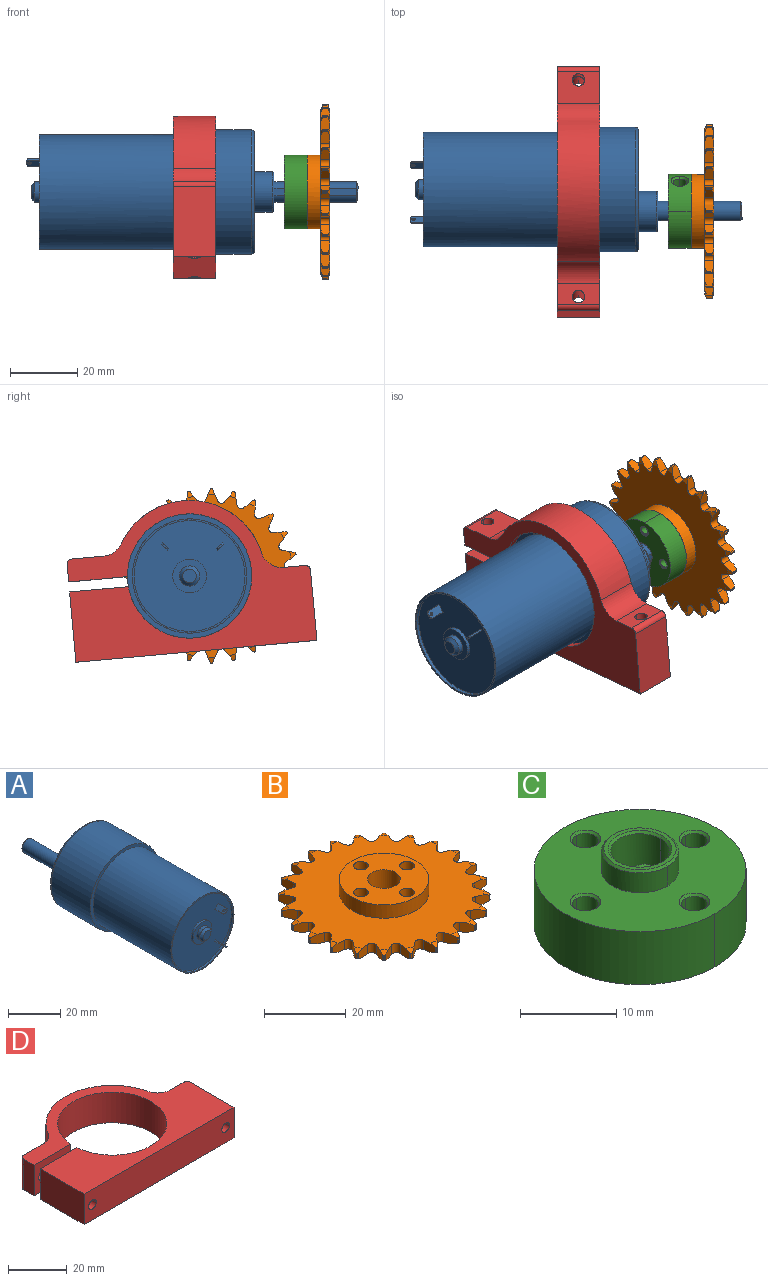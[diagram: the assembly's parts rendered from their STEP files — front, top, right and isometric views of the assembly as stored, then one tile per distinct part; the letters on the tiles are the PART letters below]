
ASSEMBLY  parts=4 mates=3
PART A: 37 faces, bbox 40.1x98.8x40.1 mm
  f0: cylinder r=3mm len=24.5mm, axis (0,-1,0), area 407.6mm2, adj f1,f3,f5
  f1: plane 24.5x2.16mm, normal (0,0,-1), area 53mm2, adj f0,f4,f5
  f2: plane 5x4.8mm, normal (0,1,0), area 19.4mm2, adj f3,f4
  f3: cone r=2.5mm half-angle=45deg, axis (0,-1,0), area 10.7mm2, adj f0,f2,f4
  f4: plane 2.17x0.51mm, normal (0,0.71,-0.71), area 1.5mm2, adj f1,f2,f3
  f5: plane 11x11mm, normal (0,1,0), area 67.1mm2, adj f0,f1,f36
  f6: plane 33x33mm, normal (0,-1,0), area 774.3mm2, adj f14,f15,f18,f19,f20,f21,f23,f24
  f7: plane 10x10mm, normal (0,-1,0), area 50.3mm2, adj f15,f16
  f8: plane 37x37mm, normal (0,-1,0), area 167.3mm2, adj f10,f12
  f9: plane 35x35mm, normal (0,1,0), area 849mm2, adj f11,f35
  f10: cylinder r=18.5mm len=37mm, axis (0,-1,0), area 2441mm2, adj f8,f35
  f11: cylinder r=6mm len=12mm, axis (0,-1,0), area 199.8mm2, adj f9,f36
  f12: cylinder r=17mm len=42mm, axis (0,1,0), area 4486.2mm2, adj f8,f13
  f13: plane 34x34mm, normal (0,-1,0), area 52.6mm2, adj f12,f14
  f14: cylinder r=16.5mm len=33mm, axis (0,-1,0), area 103.7mm2, adj f6,f13
  f15: cylinder r=5mm len=10mm, axis (0,1,0), area 31.4mm2, adj f6,f7
  f16: cylinder r=3mm len=6mm, axis (0,1,0), area 28.3mm2, adj f7,f30
  f17: plane 4x4mm, normal (0,-1,0), area 12.6mm2, adj f30
  f18: plane 4.5x0.35mm, normal (-0.71,0,-0.71), area 2.2mm2, adj f6,f19,f21,f33
  f19: plane 5x1.77mm, normal (0.71,0,-0.71), area 11.5mm2, adj f6,f18,f20,f22,f28,f33,f34
  f20: plane 4.5x0.35mm, normal (0.71,0,0.71), area 2.2mm2, adj f6,f19,f21,f34
  f21: plane 5x1.77mm, normal (-0.71,0,0.71), area 11.5mm2, adj f6,f18,f20,f22,f28,f33,f34
  f22: plane 1.41x1.41mm, normal (0,-1,0), area 0.8mm2, adj f19,f21,f33,f34
  f23: plane 4.5x0.35mm, normal (-0.71,0,0.71), area 2.3mm2, adj f6,f24,f26,f32
  f24: plane 5x1.77mm, normal (-0.71,0,-0.71), area 11.5mm2, adj f6,f23,f25,f27,f29,f31,f32
  f25: plane 4.5x0.35mm, normal (0.71,0,-0.71), area 2.2mm2, adj f6,f24,f26,f31
  f26: plane 5x1.77mm, normal (0.71,0,0.71), area 11.5mm2, adj f6,f23,f25,f27,f29,f31,f32
  f27: plane 1.41x1.41mm, normal (0,-1,0), area 0.7mm2, adj f24,f26,f31,f32
  f28: cylinder r=0.5mm len=1.06mm, axis (-0.71,0,0.71), area 1.6mm2, adj f19,f21
  f29: cylinder r=0.5mm len=1.06mm, axis (-0.71,0,-0.71), area 1.6mm2, adj f24,f26
  f30: cone r=2mm half-angle=45deg, axis (0,1,0), area 22.2mm2, adj f16,f17
  f31: plane 0.71x0.71mm, normal (0.5,-0.71,-0.5), area 0.4mm2, adj f24,f25,f26,f27
  f32: plane 0.71x0.71mm, normal (-0.5,-0.71,0.5), area 0.4mm2, adj f23,f24,f26,f27
  f33: plane 0.71x0.71mm, normal (-0.5,-0.71,-0.5), area 0.4mm2, adj f18,f19,f21,f22
  f34: plane 0.71x0.71mm, normal (0.5,-0.71,0.5), area 0.4mm2, adj f19,f20,f21,f22
  f35: torus R=17.5mm, axis (0,1,0), area 179mm2, adj f9,f10
  f36: torus R=5.5mm, axis (0,1,0), area 28.7mm2, adj f5,f11
PART B: 201 faces, bbox 52x52x6.8 mm
  f0: plane 48.65x48.65mm, normal (0,0,1), area 1311.2mm2, adj f1,f4,f7,f10,f13,f16,f19,f22
  f1: cone r=26mm half-angle=70deg, axis (0,0,-1), area 2.4mm2, adj f0,f2,f144,f146,f190,f193
  f2: cylinder r=26mm len=1.58mm, axis (0,0,1), area 0.5mm2, adj f1,f3,f190,f193
  f3: cone r=24.32mm half-angle=70deg, axis (0,0,1), area 2.4mm2, adj f2,f73,f144,f146,f190,f193
  f4: cone r=26mm half-angle=70deg, axis (0,0,-1), area 2.4mm2, adj f0,f5,f141,f143,f188,f191
  f5: cylinder r=26mm len=1.58mm, axis (0,0,1), area 0.5mm2, adj f4,f6,f188,f191
  f6: cone r=24.32mm half-angle=70deg, axis (0,0,1), area 2.4mm2, adj f5,f73,f141,f143,f188,f191
  f7: cone r=26mm half-angle=70deg, axis (0,0,-1), area 2.4mm2, adj f0,f8,f138,f140,f186,f189
  f8: cylinder r=26mm len=1.58mm, axis (0,0,1), area 0.5mm2, adj f7,f9,f186,f189
  f9: cone r=24.32mm half-angle=70deg, axis (0,0,1), area 2.4mm2, adj f8,f73,f138,f140,f186,f189
  f10: cone r=26mm half-angle=70deg, axis (0,0,-1), area 2.4mm2, adj f0,f11,f135,f137,f184,f187
  f11: cylinder r=26mm len=1.58mm, axis (0,0,1), area 0.5mm2, adj f10,f12,f184,f187
  f12: cone r=24.32mm half-angle=70deg, axis (0,0,1), area 2.4mm2, adj f11,f73,f135,f137,f184,f187
  f13: cone r=26mm half-angle=70deg, axis (0,0,-1), area 2.4mm2, adj f0,f14,f132,f134,f182,f185
  f14: cylinder r=26mm len=1.58mm, axis (0,0,1), area 0.5mm2, adj f13,f15,f182,f185
  f15: cone r=24.32mm half-angle=70deg, axis (0,0,1), area 2.4mm2, adj f14,f73,f132,f134,f182,f185
  f16: cone r=26mm half-angle=70deg, axis (0,0,-1), area 2.4mm2, adj f0,f17,f129,f131,f180,f183
  f17: cylinder r=26mm len=1.58mm, axis (0,0,1), area 0.5mm2, adj f16,f18,f180,f183
  f18: cone r=24.32mm half-angle=70deg, axis (0,0,1), area 2.4mm2, adj f17,f73,f129,f131,f180,f183
  f19: cone r=26mm half-angle=70deg, axis (0,0,-1), area 2.4mm2, adj f0,f20,f126,f128,f178,f181
  f20: cylinder r=26mm len=1.58mm, axis (0,0,1), area 0.5mm2, adj f19,f21,f178,f181
  f21: cone r=24.32mm half-angle=70deg, axis (0,0,1), area 2.4mm2, adj f20,f73,f126,f128,f178,f181
  f22: cone r=26mm half-angle=70deg, axis (0,0,-1), area 2.4mm2, adj f0,f23,f123,f125,f176,f179
  f23: cylinder r=26mm len=1.58mm, axis (0,0,1), area 0.5mm2, adj f22,f24,f176,f179
  f24: cone r=24.32mm half-angle=70deg, axis (0,0,1), area 2.4mm2, adj f23,f73,f123,f125,f176,f179
  f25: cone r=26mm half-angle=70deg, axis (0,0,-1), area 2.4mm2, adj f0,f26,f120,f122,f174,f177
  f26: cylinder r=26mm len=1.58mm, axis (0,0,1), area 0.5mm2, adj f25,f27,f174,f177
  f27: cone r=24.32mm half-angle=70deg, axis (0,0,1), area 2.4mm2, adj f26,f73,f120,f122,f174,f177
  f28: cone r=26mm half-angle=70deg, axis (0,0,-1), area 2.4mm2, adj f0,f29,f117,f119,f172,f175
  f29: cylinder r=26mm len=1.58mm, axis (0,0,1), area 0.5mm2, adj f28,f30,f172,f175
  f30: cone r=24.32mm half-angle=70deg, axis (0,0,1), area 2.4mm2, adj f29,f73,f117,f119,f172,f175
  f31: cone r=26mm half-angle=70deg, axis (0,0,-1), area 2.4mm2, adj f0,f32,f114,f116,f170,f173
  f32: cylinder r=26mm len=1.58mm, axis (0,0,1), area 0.5mm2, adj f31,f33,f170,f173
  f33: cone r=24.32mm half-angle=70deg, axis (0,0,1), area 2.4mm2, adj f32,f73,f114,f116,f170,f173
  f34: cone r=26mm half-angle=70deg, axis (0,0,-1), area 2.4mm2, adj f0,f35,f111,f113,f168,f171
  f35: cylinder r=26mm len=1.58mm, axis (0,0,1), area 0.5mm2, adj f34,f36,f168,f171
  f36: cone r=24.32mm half-angle=70deg, axis (0,0,1), area 2.4mm2, adj f35,f73,f111,f113,f168,f171
  f37: cone r=26mm half-angle=70deg, axis (0,0,-1), area 2.4mm2, adj f0,f38,f108,f110,f166,f169
  f38: cylinder r=26mm len=1.58mm, axis (0,0,1), area 0.5mm2, adj f37,f39,f166,f169
  f39: cone r=24.32mm half-angle=70deg, axis (0,0,1), area 2.4mm2, adj f38,f73,f108,f110,f166,f169
  f40: cone r=26mm half-angle=70deg, axis (0,0,-1), area 2.4mm2, adj f0,f41,f105,f107,f164,f167
  f41: cylinder r=26mm len=1.58mm, axis (0,0,1), area 0.5mm2, adj f40,f42,f164,f167
  f42: cone r=24.32mm half-angle=70deg, axis (0,0,1), area 2.4mm2, adj f41,f73,f105,f107,f164,f167
  f43: cone r=26mm half-angle=70deg, axis (0,0,-1), area 2.4mm2, adj f0,f44,f102,f104,f162,f165
  f44: cylinder r=26mm len=1.58mm, axis (0,0,1), area 0.5mm2, adj f43,f45,f162,f165
  f45: cone r=24.32mm half-angle=70deg, axis (0,0,1), area 2.4mm2, adj f44,f73,f102,f104,f162,f165
  f46: cone r=26mm half-angle=70deg, axis (0,0,-1), area 2.4mm2, adj f0,f47,f99,f101,f160,f163
  f47: cylinder r=26mm len=1.58mm, axis (0,0,1), area 0.5mm2, adj f46,f48,f160,f163
  f48: cone r=24.32mm half-angle=70deg, axis (0,0,1), area 2.4mm2, adj f47,f73,f99,f101,f160,f163
  f49: cone r=26mm half-angle=70deg, axis (0,0,-1), area 2.4mm2, adj f0,f50,f96,f98,f158,f161
  f50: cylinder r=26mm len=1.58mm, axis (0,0,1), area 0.5mm2, adj f49,f51,f158,f161
  f51: cone r=24.32mm half-angle=70deg, axis (0,0,1), area 2.4mm2, adj f50,f73,f96,f98,f158,f161
  f52: cone r=26mm half-angle=70deg, axis (0,0,-1), area 2.4mm2, adj f0,f53,f93,f95,f156,f159
  f53: cylinder r=26mm len=1.58mm, axis (0,0,1), area 0.5mm2, adj f52,f54,f156,f159
  f54: cone r=24.32mm half-angle=70deg, axis (0,0,1), area 2.4mm2, adj f53,f73,f93,f95,f156,f159
  f55: cone r=26mm half-angle=70deg, axis (0,0,-1), area 2.4mm2, adj f0,f56,f90,f92,f154,f157
  f56: cylinder r=26mm len=1.58mm, axis (0,0,1), area 0.5mm2, adj f55,f57,f154,f157
  f57: cone r=24.32mm half-angle=70deg, axis (0,0,1), area 2.4mm2, adj f56,f73,f90,f92,f154,f157
  f58: cone r=26mm half-angle=70deg, axis (0,0,-1), area 2.4mm2, adj f0,f59,f87,f89,f152,f155
  f59: cylinder r=26mm len=1.58mm, axis (0,0,1), area 0.5mm2, adj f58,f60,f152,f155
  f60: cone r=24.32mm half-angle=70deg, axis (0,0,1), area 2.4mm2, adj f59,f73,f87,f89,f152,f155
  f61: cone r=26mm half-angle=70deg, axis (0,0,-1), area 2.4mm2, adj f0,f62,f84,f86,f150,f153
  f62: cylinder r=26mm len=1.58mm, axis (0,0,1), area 0.5mm2, adj f61,f63,f150,f153
  f63: cone r=24.32mm half-angle=70deg, axis (0,0,1), area 2.4mm2, adj f62,f73,f84,f86,f150,f153
  f64: cone r=26mm half-angle=70deg, axis (0,0,-1), area 2.4mm2, adj f0,f65,f81,f83,f148,f151
  f65: cylinder r=26mm len=1.58mm, axis (0,0,1), area 0.5mm2, adj f64,f66,f148,f151
  f66: cone r=24.32mm half-angle=70deg, axis (0,0,1), area 2.4mm2, adj f65,f73,f81,f83,f148,f151
  f67: cone r=26mm half-angle=70deg, axis (0,0,-1), area 2.4mm2, adj f0,f68,f76,f77,f80,f149
  f68: cylinder r=26mm len=1.58mm, axis (0,0,1), area 0.5mm2, adj f67,f69,f77,f149
  f69: cone r=24.32mm half-angle=70deg, axis (0,0,1), area 2.4mm2, adj f68,f73,f76,f77,f80,f149
  f70: cone r=26mm half-angle=70deg, axis (0,0,-1), area 2.4mm2, adj f0,f71,f75,f78,f147,f192
  f71: cylinder r=26mm len=1.58mm, axis (0,0,1), area 0.5mm2, adj f70,f72,f78,f192
  f72: cone r=24.32mm half-angle=70deg, axis (0,0,1), area 2.4mm2, adj f71,f73,f75,f78,f147,f192
  f73: plane 48.65x48.65mm, normal (0,0,-1), area 1600.4mm2, adj f3,f6,f9,f12,f15,f18,f21,f24
  f74: cylinder r=1.25mm len=2.8mm, axis (0,0,1), area 7.2mm2, adj f0,f73,f75,f76
  f75: plane 2.99x2.8mm, normal (0.78,0.62,0), area 9.7mm2, adj f0,f70,f72,f73,f74,f78
  f76: plane 3.5x2.8mm, normal (-0.92,0.4,0), area 9.7mm2, adj f0,f67,f69,f73,f74,f77
  f77: cylinder r=0.2mm len=1.67mm, axis (0,0,1), area 0.4mm2, adj f67,f68,f69,f76
  f78: cylinder r=0.2mm len=1.67mm, axis (0,0,1), area 0.4mm2, adj f70,f71,f72,f75
  f79: cylinder r=1.25mm len=2.8mm, axis (0,0,1), area 7.2mm2, adj f0,f73,f80,f81
  f80: plane 3.5x2.8mm, normal (0.92,0.4,0), area 9.7mm2, adj f0,f67,f69,f73,f79,f149
  f81: plane 2.99x2.8mm, normal (-0.78,0.62,0), area 9.7mm2, adj f0,f64,f66,f73,f79,f148
  f82: cylinder r=1.25mm len=2.8mm, axis (0,0,1), area 7.2mm2, adj f0,f73,f83,f84
  f83: plane 3.77x2.8mm, normal (0.99,0.15,0), area 9.7mm2, adj f0,f64,f66,f73,f82,f151
  f84: plane 3.06x2.8mm, normal (-0.6,0.8,0), area 9.7mm2, adj f0,f61,f63,f73,f82,f150
  f85: cylinder r=1.25mm len=2.8mm, axis (0,0,1), area 7.2mm2, adj f0,f73,f86,f87
  f86: plane 3.79x2.8mm, normal (0.99,-0.12,0), area 9.7mm2, adj f0,f61,f63,f73,f85,f153
  f87: plane 3.54x2.8mm, normal (-0.37,0.93,0), area 9.7mm2, adj f0,f58,f60,f73,f85,f152
  f88: cylinder r=1.25mm len=2.8mm, axis (0,0,1), area 7.2mm2, adj f0,f73,f89,f90
  f89: plane 3.54x2.8mm, normal (0.93,-0.37,0), area 9.7mm2, adj f0,f58,f60,f73,f88,f155
  f90: plane 3.79x2.8mm, normal (-0.12,0.99,0), area 9.7mm2, adj f0,f55,f57,f73,f88,f154
  f91: cylinder r=1.25mm len=2.8mm, axis (0,0,1), area 7.2mm2, adj f0,f73,f92,f93
  f92: plane 3.06x2.8mm, normal (0.8,-0.6,0), area 9.7mm2, adj f0,f55,f57,f73,f91,f157
  f93: plane 3.77x2.8mm, normal (0.15,0.99,0), area 9.7mm2, adj f0,f52,f54,f73,f91,f156
  f94: cylinder r=1.25mm len=2.8mm, axis (0,0,1), area 7.2mm2, adj f0,f73,f95,f96
  f95: plane 2.99x2.8mm, normal (0.62,-0.78,0), area 9.7mm2, adj f0,f52,f54,f73,f94,f159
  f96: plane 3.5x2.8mm, normal (0.4,0.92,0), area 9.7mm2, adj f0,f49,f51,f73,f94,f158
  f97: cylinder r=1.25mm len=2.8mm, axis (0,0,1), area 7.2mm2, adj f0,f73,f98,f99
  f98: plane 3.5x2.8mm, normal (0.4,-0.92,0), area 9.7mm2, adj f0,f49,f51,f73,f97,f161
  f99: plane 2.99x2.8mm, normal (0.62,0.78,0), area 9.7mm2, adj f0,f46,f48,f73,f97,f160
  f100: cylinder r=1.25mm len=2.8mm, axis (0,0,1), area 7.2mm2, adj f0,f73,f101,f102
  f101: plane 3.77x2.8mm, normal (0.15,-0.99,0), area 9.7mm2, adj f0,f46,f48,f73,f100,f163
  f102: plane 3.06x2.8mm, normal (0.8,0.6,0), area 9.7mm2, adj f0,f43,f45,f73,f100,f162
  f103: cylinder r=1.25mm len=2.8mm, axis (0,0,1), area 7.2mm2, adj f0,f73,f104,f105
  f104: plane 3.79x2.8mm, normal (-0.12,-0.99,0), area 9.7mm2, adj f0,f43,f45,f73,f103,f165
  f105: plane 3.54x2.8mm, normal (0.93,0.37,0), area 9.7mm2, adj f0,f40,f42,f73,f103,f164
  f106: cylinder r=1.25mm len=2.8mm, axis (0,0,1), area 7.2mm2, adj f0,f73,f107,f108
  f107: plane 3.54x2.8mm, normal (-0.37,-0.93,0), area 9.7mm2, adj f0,f40,f42,f73,f106,f167
  f108: plane 3.79x2.8mm, normal (0.99,0.12,0), area 9.7mm2, adj f0,f37,f39,f73,f106,f166
  f109: cylinder r=1.25mm len=2.8mm, axis (0,0,1), area 7.2mm2, adj f0,f73,f110,f111
  f110: plane 3.06x2.8mm, normal (-0.6,-0.8,0), area 9.7mm2, adj f0,f37,f39,f73,f109,f169
  f111: plane 3.77x2.8mm, normal (0.99,-0.15,0), area 9.7mm2, adj f0,f34,f36,f73,f109,f168
  f112: cylinder r=1.25mm len=2.8mm, axis (0,0,1), area 7.2mm2, adj f0,f73,f113,f114
  f113: plane 2.99x2.8mm, normal (-0.78,-0.62,0), area 9.7mm2, adj f0,f34,f36,f73,f112,f171
  f114: plane 3.5x2.8mm, normal (0.92,-0.4,0), area 9.7mm2, adj f0,f31,f33,f73,f112,f170
  f115: cylinder r=1.25mm len=2.8mm, axis (0,0,1), area 7.2mm2, adj f0,f73,f116,f117
  f116: plane 3.5x2.8mm, normal (-0.92,-0.4,0), area 9.7mm2, adj f0,f31,f33,f73,f115,f173
  f117: plane 2.99x2.8mm, normal (0.78,-0.62,0), area 9.7mm2, adj f0,f28,f30,f73,f115,f172
  f118: cylinder r=1.25mm len=2.8mm, axis (0,0,1), area 7.2mm2, adj f0,f73,f119,f120
  f119: plane 3.77x2.8mm, normal (-0.99,-0.15,0), area 9.7mm2, adj f0,f28,f30,f73,f118,f175
  f120: plane 3.06x2.8mm, normal (0.6,-0.8,0), area 9.7mm2, adj f0,f25,f27,f73,f118,f174
  f121: cylinder r=1.25mm len=2.8mm, axis (0,0,1), area 7.2mm2, adj f0,f73,f122,f123
  f122: plane 3.79x2.8mm, normal (-0.99,0.12,0), area 9.7mm2, adj f0,f25,f27,f73,f121,f177
  f123: plane 3.54x2.8mm, normal (0.37,-0.93,0), area 9.7mm2, adj f0,f22,f24,f73,f121,f176
  f124: cylinder r=1.25mm len=2.8mm, axis (0,0,1), area 7.2mm2, adj f0,f73,f125,f126
  f125: plane 3.54x2.8mm, normal (-0.93,0.37,0), area 9.7mm2, adj f0,f22,f24,f73,f124,f179
  f126: plane 3.79x2.8mm, normal (0.12,-0.99,0), area 9.7mm2, adj f0,f19,f21,f73,f124,f178
  f127: cylinder r=1.25mm len=2.8mm, axis (0,0,1), area 7.2mm2, adj f0,f73,f128,f129
  f128: plane 3.06x2.8mm, normal (-0.8,0.6,0), area 9.7mm2, adj f0,f19,f21,f73,f127,f181
  f129: plane 3.77x2.8mm, normal (-0.15,-0.99,0), area 9.7mm2, adj f0,f16,f18,f73,f127,f180
  f130: cylinder r=1.25mm len=2.8mm, axis (0,0,1), area 7.2mm2, adj f0,f73,f131,f132
  f131: plane 2.99x2.8mm, normal (-0.62,0.78,0), area 9.7mm2, adj f0,f16,f18,f73,f130,f183
  f132: plane 3.5x2.8mm, normal (-0.4,-0.92,0), area 9.7mm2, adj f0,f13,f15,f73,f130,f182
  f133: cylinder r=1.25mm len=2.8mm, axis (0,0,1), area 7.2mm2, adj f0,f73,f134,f135
  f134: plane 3.5x2.8mm, normal (-0.4,0.92,0), area 9.7mm2, adj f0,f13,f15,f73,f133,f185
  f135: plane 2.99x2.8mm, normal (-0.62,-0.78,0), area 9.7mm2, adj f0,f10,f12,f73,f133,f184
  f136: cylinder r=1.25mm len=2.8mm, axis (0,0,1), area 7.2mm2, adj f0,f73,f137,f138
  f137: plane 3.77x2.8mm, normal (-0.15,0.99,0), area 9.7mm2, adj f0,f10,f12,f73,f136,f187
  f138: plane 3.06x2.8mm, normal (-0.8,-0.6,0), area 9.7mm2, adj f0,f7,f9,f73,f136,f186
  f139: cylinder r=1.25mm len=2.8mm, axis (0,0,1), area 7.2mm2, adj f0,f73,f140,f141
  f140: plane 3.79x2.8mm, normal (0.12,0.99,0), area 9.7mm2, adj f0,f7,f9,f73,f139,f189
  f141: plane 3.54x2.8mm, normal (-0.93,-0.37,0), area 9.7mm2, adj f0,f4,f6,f73,f139,f188
  f142: cylinder r=1.25mm len=2.8mm, axis (0,0,1), area 7.2mm2, adj f0,f73,f143,f144
  f143: plane 3.54x2.8mm, normal (0.37,0.93,0), area 9.7mm2, adj f0,f4,f6,f73,f142,f191
  f144: plane 3.79x2.8mm, normal (-0.99,-0.12,0), area 9.7mm2, adj f0,f1,f3,f73,f142,f190
  f145: cylinder r=1.25mm len=2.8mm, axis (0,0,1), area 7.2mm2, adj f0,f73,f146,f147
  f146: plane 3.06x2.8mm, normal (0.6,0.8,0), area 9.7mm2, adj f0,f1,f3,f73,f145,f193
  f147: plane 3.77x2.8mm, normal (-0.99,0.15,0), area 9.7mm2, adj f0,f70,f72,f73,f145,f192
  f148: cylinder r=0.2mm len=1.67mm, axis (0,0,1), area 0.4mm2, adj f64,f65,f66,f81
  f149: cylinder r=0.2mm len=1.67mm, axis (0,0,1), area 0.4mm2, adj f67,f68,f69,f80
  f150: cylinder r=0.2mm len=1.67mm, axis (0,0,1), area 0.4mm2, adj f61,f62,f63,f84
  f151: cylinder r=0.2mm len=1.67mm, axis (0,0,1), area 0.4mm2, adj f64,f65,f66,f83
  f152: cylinder r=0.2mm len=1.67mm, axis (0,0,1), area 0.4mm2, adj f58,f59,f60,f87
  f153: cylinder r=0.2mm len=1.67mm, axis (0,0,1), area 0.4mm2, adj f61,f62,f63,f86
  f154: cylinder r=0.2mm len=1.67mm, axis (0,0,1), area 0.4mm2, adj f55,f56,f57,f90
  f155: cylinder r=0.2mm len=1.67mm, axis (0,0,1), area 0.4mm2, adj f58,f59,f60,f89
  f156: cylinder r=0.2mm len=1.67mm, axis (0,0,1), area 0.4mm2, adj f52,f53,f54,f93
  f157: cylinder r=0.2mm len=1.67mm, axis (0,0,1), area 0.4mm2, adj f55,f56,f57,f92
  f158: cylinder r=0.2mm len=1.67mm, axis (0,0,1), area 0.4mm2, adj f49,f50,f51,f96
  f159: cylinder r=0.2mm len=1.67mm, axis (0,0,1), area 0.4mm2, adj f52,f53,f54,f95
  f160: cylinder r=0.2mm len=1.67mm, axis (0,0,1), area 0.4mm2, adj f46,f47,f48,f99
  f161: cylinder r=0.2mm len=1.67mm, axis (0,0,1), area 0.4mm2, adj f49,f50,f51,f98
  f162: cylinder r=0.2mm len=1.67mm, axis (0,0,1), area 0.4mm2, adj f43,f44,f45,f102
  f163: cylinder r=0.2mm len=1.67mm, axis (0,0,1), area 0.4mm2, adj f46,f47,f48,f101
  f164: cylinder r=0.2mm len=1.67mm, axis (0,0,1), area 0.4mm2, adj f40,f41,f42,f105
  f165: cylinder r=0.2mm len=1.67mm, axis (0,0,1), area 0.4mm2, adj f43,f44,f45,f104
  f166: cylinder r=0.2mm len=1.67mm, axis (0,0,1), area 0.4mm2, adj f37,f38,f39,f108
  f167: cylinder r=0.2mm len=1.67mm, axis (0,0,1), area 0.4mm2, adj f40,f41,f42,f107
  f168: cylinder r=0.2mm len=1.67mm, axis (0,0,1), area 0.4mm2, adj f34,f35,f36,f111
  f169: cylinder r=0.2mm len=1.67mm, axis (0,0,1), area 0.4mm2, adj f37,f38,f39,f110
  f170: cylinder r=0.2mm len=1.67mm, axis (0,0,1), area 0.4mm2, adj f31,f32,f33,f114
  f171: cylinder r=0.2mm len=1.67mm, axis (0,0,1), area 0.4mm2, adj f34,f35,f36,f113
  f172: cylinder r=0.2mm len=1.67mm, axis (0,0,1), area 0.4mm2, adj f28,f29,f30,f117
  f173: cylinder r=0.2mm len=1.67mm, axis (0,0,1), area 0.4mm2, adj f31,f32,f33,f116
  f174: cylinder r=0.2mm len=1.67mm, axis (0,0,1), area 0.4mm2, adj f25,f26,f27,f120
  f175: cylinder r=0.2mm len=1.67mm, axis (0,0,1), area 0.4mm2, adj f28,f29,f30,f119
  f176: cylinder r=0.2mm len=1.67mm, axis (0,0,1), area 0.4mm2, adj f22,f23,f24,f123
  f177: cylinder r=0.2mm len=1.67mm, axis (0,0,1), area 0.4mm2, adj f25,f26,f27,f122
  f178: cylinder r=0.2mm len=1.67mm, axis (0,0,1), area 0.4mm2, adj f19,f20,f21,f126
  f179: cylinder r=0.2mm len=1.67mm, axis (0,0,1), area 0.4mm2, adj f22,f23,f24,f125
  f180: cylinder r=0.2mm len=1.67mm, axis (0,0,1), area 0.4mm2, adj f16,f17,f18,f129
  f181: cylinder r=0.2mm len=1.67mm, axis (0,0,1), area 0.4mm2, adj f19,f20,f21,f128
  f182: cylinder r=0.2mm len=1.67mm, axis (0,0,1), area 0.4mm2, adj f13,f14,f15,f132
  f183: cylinder r=0.2mm len=1.67mm, axis (0,0,1), area 0.4mm2, adj f16,f17,f18,f131
  f184: cylinder r=0.2mm len=1.67mm, axis (0,0,1), area 0.4mm2, adj f10,f11,f12,f135
  f185: cylinder r=0.2mm len=1.67mm, axis (0,0,1), area 0.4mm2, adj f13,f14,f15,f134
  f186: cylinder r=0.2mm len=1.67mm, axis (0,0,1), area 0.4mm2, adj f7,f8,f9,f138
  f187: cylinder r=0.2mm len=1.67mm, axis (0,0,1), area 0.4mm2, adj f10,f11,f12,f137
  f188: cylinder r=0.2mm len=1.67mm, axis (0,0,1), area 0.4mm2, adj f4,f5,f6,f141
  f189: cylinder r=0.2mm len=1.67mm, axis (0,0,1), area 0.4mm2, adj f7,f8,f9,f140
  f190: cylinder r=0.2mm len=1.67mm, axis (0,0,1), area 0.4mm2, adj f1,f2,f3,f144
  f191: cylinder r=0.2mm len=1.67mm, axis (0,0,1), area 0.4mm2, adj f4,f5,f6,f143
  f192: cylinder r=0.2mm len=1.67mm, axis (0,0,1), area 0.4mm2, adj f70,f71,f72,f147
  f193: cylinder r=0.2mm len=1.67mm, axis (0,0,1), area 0.4mm2, adj f1,f2,f3,f146
  f194: cylinder r=11mm len=22mm, axis (0,0,-1), area 276.5mm2, adj f0,f195
  f195: plane 22x22mm, normal (0,0,1), area 289.2mm2, adj f194,f196,f197,f198,f199,f200
  f196: cylinder r=4mm len=8mm, axis (0,0,1), area 170.9mm2, adj f73,f195
  f197: cylinder r=1.8mm len=6.8mm, axis (0,0,1), area 76.9mm2, adj f73,f195
  f198: cylinder r=1.8mm len=6.8mm, axis (0,0,1), area 76.9mm2, adj f73,f195
  f199: cylinder r=1.8mm len=6.8mm, axis (0,0,1), area 76.9mm2, adj f73,f195
  f200: cylinder r=1.8mm len=6.8mm, axis (0,0,1), area 76.9mm2, adj f73,f195
PART C: 43 faces, bbox 22x22x9.5 mm
  f0: cylinder r=3.05mm len=9mm, axis (0,0,-1), area 85.7mm2, adj f1,f2,f4,f5,f6
  f1: cylinder r=3.05mm len=9mm, axis (0,0,-1), area 73.3mm2, adj f0,f3,f4,f5,f7
  f2: cone r=0mm half-angle=45deg, axis (0,0,1), area 3.5mm2, adj f0,f3,f8
  f3: cone r=0mm half-angle=45deg, axis (0,0,1), area 3.5mm2, adj f1,f2,f8
  f4: cylinder r=2.02mm len=8.72mm, axis (0.84,0.54,0), area 48.5mm2, adj f0,f1,f5,f17
  f5: cylinder r=2.02mm len=8.72mm, axis (0.84,0.54,0), area 48.5mm2, adj f0,f1,f4,f18
  f6: cone r=0mm half-angle=45deg, axis (0,0,-1), area 3.5mm2, adj f0,f7,f19
  f7: cone r=0mm half-angle=45deg, axis (0,0,-1), area 3.5mm2, adj f1,f6,f19
  f8: plane 7.52x7.5mm, normal (0,0,1), area 10mm2, adj f2,f3,f20,f21
  f9: cone r=0mm half-angle=45deg, axis (0,0,-1), area 1.6mm2, adj f10,f19,f22
  f10: cone r=0mm half-angle=45deg, axis (0,0,-1), area 1.6mm2, adj f9,f19,f23
  f11: cone r=0mm half-angle=45deg, axis (0,0,-1), area 1.6mm2, adj f12,f19,f24
  f12: cone r=0mm half-angle=45deg, axis (0,0,-1), area 1.6mm2, adj f11,f19,f25
  f13: cone r=0mm half-angle=45deg, axis (0,0,-1), area 1.6mm2, adj f14,f19,f26
  f14: cone r=0mm half-angle=45deg, axis (0,0,-1), area 1.6mm2, adj f13,f19,f27
  f15: cone r=0mm half-angle=45deg, axis (0,0,-1), area 1.6mm2, adj f16,f19,f28
  f16: cone r=0mm half-angle=45deg, axis (0,0,-1), area 1.6mm2, adj f15,f19,f29
  f17: bspline ~4.65x3.1mm, area 6.7mm2, adj f4,f18,f30
  f18: bspline ~4.65x3.1mm, area 6.7mm2, adj f5,f17,f30
  f19: plane 22.04x22mm, normal (0,0,-1), area 313.6mm2, adj f6,f7,f9,f10,f11,f12,f13,f14
  f20: cone r=0mm half-angle=45deg, axis (0,0,-1), area 4.3mm2, adj f8,f21,f32
  f21: cone r=0mm half-angle=45deg, axis (0,0,-1), area 4.3mm2, adj f8,f20,f33
  f22: cylinder r=1.35mm len=6.25mm, axis (0,0,-1), area 26.6mm2, adj f9,f23,f34
  f23: cylinder r=1.35mm len=6.25mm, axis (0,0,-1), area 26.6mm2, adj f10,f22,f35
  f24: cylinder r=1.35mm len=6.25mm, axis (0,0,-1), area 26.6mm2, adj f11,f25,f36
  f25: cylinder r=1.35mm len=6.25mm, axis (0,0,-1), area 26.6mm2, adj f12,f24,f37
  f26: cylinder r=1.35mm len=6.25mm, axis (0,0,-1), area 26.6mm2, adj f13,f27,f38
  f27: cylinder r=1.35mm len=6.25mm, axis (0,0,-1), area 26.6mm2, adj f14,f26,f39
  f28: cylinder r=1.35mm len=6.25mm, axis (0,0,-1), area 26.6mm2, adj f15,f29,f40
  f29: cylinder r=1.35mm len=6.25mm, axis (0,0,-1), area 26.6mm2, adj f16,f28,f41
  f30: cylinder r=11mm len=22mm, axis (0,0,1), area 210.3mm2, adj f17,f18,f19,f31,f42
  f31: cylinder r=11mm len=22mm, axis (0,0,1), area 233.3mm2, adj f19,f30,f42
  f32: cylinder r=4mm len=8mm, axis (0,0,1), area 31.4mm2, adj f20,f33,f42
  f33: cylinder r=4mm len=8mm, axis (0,0,1), area 31.4mm2, adj f21,f32,f42
  f34: cone r=0mm half-angle=45deg, axis (0,0,1), area 1.6mm2, adj f22,f35,f42
  f35: cone r=0mm half-angle=45deg, axis (0,0,1), area 1.6mm2, adj f23,f34,f42
  f36: cone r=0mm half-angle=45deg, axis (0,0,1), area 1.6mm2, adj f24,f37,f42
  f37: cone r=0mm half-angle=45deg, axis (0,0,1), area 1.6mm2, adj f25,f36,f42
  f38: cone r=0mm half-angle=45deg, axis (0,0,1), area 1.6mm2, adj f26,f39,f42
  f39: cone r=0mm half-angle=45deg, axis (0,0,1), area 1.6mm2, adj f27,f38,f42
  f40: cone r=0mm half-angle=45deg, axis (0,0,1), area 1.6mm2, adj f28,f41,f42
  f41: cone r=0mm half-angle=45deg, axis (0,0,1), area 1.6mm2, adj f29,f40,f42
  f42: plane 22.04x22mm, normal (0,0,1), area 297.6mm2, adj f30,f31,f32,f33,f34,f35,f36,f37
PART D: 22 faces, bbox 72x45x12.7 mm
  f0: cylinder r=1.85mm len=6.7mm, axis (0,-1,0), area 38.9mm2, adj f1,f12,f15
  f1: cylinder r=1.85mm len=6.7mm, axis (0,-1,0), area 38.9mm2, adj f0,f12,f15
  f2: cylinder r=1.85mm len=22.5mm, axis (0,-1,0), area 130.8mm2, adj f3,f8,f19
  f3: cylinder r=1.85mm len=22.5mm, axis (0,-1,0), area 130.8mm2, adj f2,f8,f19
  f4: cylinder r=1.85mm len=21mm, axis (0,-1,0), area 122.1mm2, adj f5,f17,f19
  f5: cylinder r=1.85mm len=21mm, axis (0,-1,0), area 122.1mm2, adj f4,f17,f19
  f6: plane 72x45.04mm, normal (0,0,1), area 1409.8mm2, adj f7,f8,f9,f10,f11,f12,f13,f14
  f7: cylinder r=1.5mm len=12.7mm, axis (0,0,-1), area 29.9mm2, adj f6,f8,f20,f21
  f8: plane 12.7x6.36mm, normal (0,1,0), area 70mm2, adj f2,f3,f6,f7,f9,f21
  f9: cylinder r=6.35mm len=12.7mm, axis (0,0,1), area 108.8mm2, adj f6,f8,f10,f21
  f10: cylinder r=22.5mm len=41.38mm, axis (0,0,1), area 683.2mm2, adj f6,f9,f11,f21
  f11: cylinder r=6.35mm len=12.7mm, axis (0,0,1), area 84mm2, adj f6,f10,f12,f21
  f12: plane 12.7x9.59mm, normal (0,1,0), area 111mm2, adj f0,f1,f6,f11,f13,f21
  f13: cylinder r=1.5mm len=12.7mm, axis (0,0,-1), area 29.9mm2, adj f6,f12,f14,f21
  f14: plane 12.7x5.2mm, normal (-1,0,0), area 66mm2, adj f6,f13,f15,f21
  f15: plane 17.56x12.7mm, normal (0,-1,0), area 212.3mm2, adj f0,f1,f6,f14,f16,f21
  f16: cylinder r=18.5mm len=37mm, axis (0,0,1), area 1438.1mm2, adj f6,f15,f17,f21
  f17: plane 17.56x12.7mm, normal (0,1,0), area 212.3mm2, adj f4,f5,f6,f16,f18,f21
  f18: plane 21x12.7mm, normal (-1,0,0), area 266.7mm2, adj f6,f17,f19,f21
  f19: plane 72x12.7mm, normal (0,-1,0), area 892.9mm2, adj f2,f3,f4,f5,f6,f18,f20,f21
  f20: plane 21x12.7mm, normal (1,0,0), area 266.7mm2, adj f6,f7,f19,f21
  f21: plane 72x45.04mm, normal (0,0,-1), area 1409.8mm2, adj f7,f8,f9,f10,f11,f12,f13,f14
PLACE A rot(axis=(-0.58,-0.58,-0.58),120deg) t=(313.12,657.63,-653.48)mm
PLACE B rot(axis=(-0.58,-0.58,0.58),120deg) t=(354.78,651.13,-653.48)mm
PLACE C rot(axis=(0.58,0.58,0.58),120deg) t=(350.78,651.13,-653.48)mm
PLACE D rot(axis=(0.56,-0.61,-0.56),117deg) t=(317.27,657.63,-653.48)mm
MATE fastened C.f20 <-> B.f1  axis (1,0,0) through (350.78,651.13,-653.48)mm
MATE revolute A.f10 <-> D.f10  axis (-1,0,0) through (323.62,657.63,-653.48)mm
MATE slider C.f20 <-> A.f0  axis (-1,0,0) through (344.03,651.13,-653.48)mm
